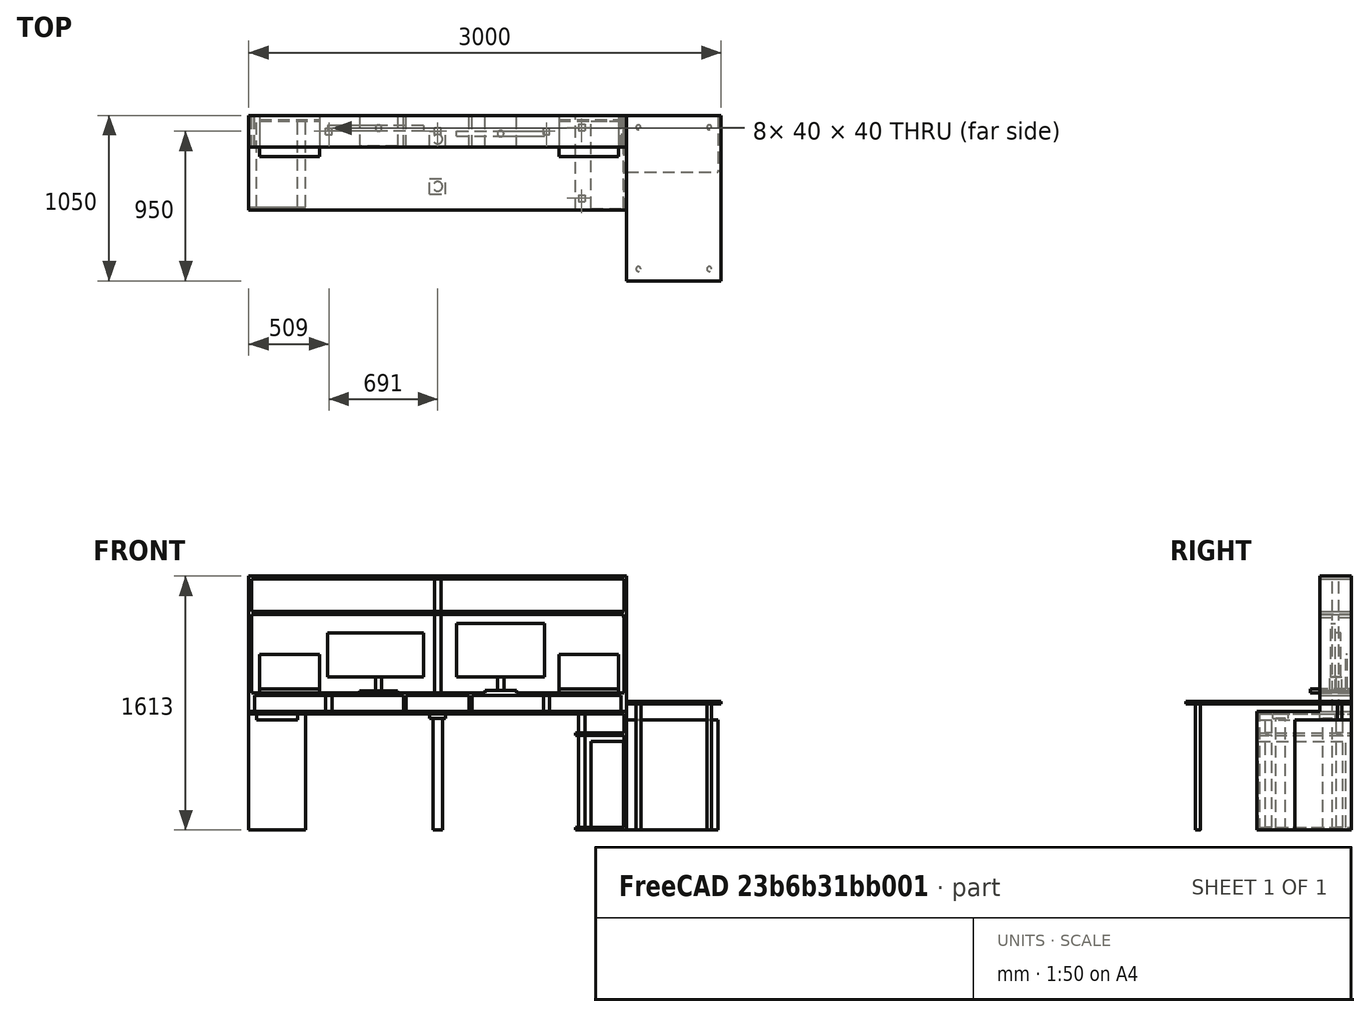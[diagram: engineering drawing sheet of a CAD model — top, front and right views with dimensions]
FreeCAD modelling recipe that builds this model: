
FCSTD DOCUMENT  (FreeCAD 0.16R6712 (Git))
Label: double-desk-240-300
License: All rights reserved
LicenseURL: http://en.wikipedia.org/wiki/All_rights_reserved
objects: Part::Box×43, Part::Cylinder×8, Part::MultiFuse×8, Drawing::FeatureViewPart×4, Drawing::FeaturePage×1
note: 59 computed .brp shape members not serialized (recipe doc carries the construction recipe); baked Part::Feature solids carry a one-line shape summary decoded from their .brp

FEATURE [Part::Box] Box  label="Base"
  Height = 18
  Length = 2400
  Placement = pos=(0,0,736) rot=(0,0,1;0rad)
  Width = 600
FEATURE [Part::Box] Box001  label="IkeaALEX"
  Height = 700
  Length = 360
  Placement = pos=(0,20,0) rot=(0,0,1;0rad)
  Width = 580
FEATURE [Part::Box] Box002  label="R"
  Height = 718
  Length = 18
  Placement = pos=(2382,0,18) rot=(0,0,1;0rad)
  Width = 600
FEATURE [Part::Box] Box003  label="Balda_1"
  Height = 18
  Length = 2364
  Placement = pos=(18,400,854) rot=(0,0,1;0rad)
  Width = 200
FEATURE [Part::Box] Box004  label="Balda_2"
  Height = 18
  Length = 2364
  Placement = pos=(18,400,1369) rot=(0,0,1;0rad)
  Width = 200
FEATURE [Part::Box] Box005  label="Balda_3"
  Height = 18
  Length = 2400
  Placement = pos=(0,400,1595) rot=(0,0,1;0rad)
  Width = 200
FEATURE [Part::Box] Box006  label="Balda_l"
  Height = 841
  Length = 18
  Placement = pos=(0,400,754) rot=(0,0,1;0rad)
  Width = 200
FEATURE [Part::Box] Box007  label="Balda_r"
  Height = 841
  Length = 18
  Placement = pos=(2382,400,754) rot=(0,0,1;0rad)
  Width = 200
FEATURE [Part::Cylinder] Cylinder  label="Leg710C_1"
  Angle = 360
  Height = 710
  Placement = pos=(1200,450,0) rot=(0,0,1;0rad)
  Radius = 30
FEATURE [Part::Cylinder] Cylinder001  label="Leg710C_2"
  Angle = 360
  Height = 710
  Placement = pos=(1200,150,0) rot=(0,0,1;0rad)
  Radius = 30
FEATURE [Part::Box] Box008  label="FixBalda_1l"
  Height = 100
  Length = 18
  Placement = pos=(18,400,754) rot=(0,0,1;0rad)
  Width = 200
FEATURE [Part::Box] Box009  label="FixBalda_1r"
  Height = 100
  Length = 18
  Placement = pos=(2364,400,754) rot=(0,0,1;0rad)
  Width = 200
FEATURE [Part::Box] Box010  label="FixALEX_lb"
  Height = 18
  Length = 50
  Placement = pos=(0,20,700) rot=(0,0,1;0rad)
  Width = 580
FEATURE [Part::Box] Box011  label="FixALEX_lt"
  Height = 18
  Length = 50
  Placement = pos=(0,20,718) rot=(0,0,1;0rad)
  Width = 580
FEATURE [Part::Box] Box012  label="FixALEX_rb"
  Height = 18
  Length = 50
  Placement = pos=(310,20,700) rot=(0,0,1;0rad)
  Width = 580
FEATURE [Part::Box] Box013  label="FixALEX_rt"
  Height = 18
  Length = 50
  Placement = pos=(310,20,718) rot=(0,0,1;0rad)
  Width = 580
FEATURE [Part::Box] Box014  label="FixLeg710C_1b"
  Height = 18
  Length = 100
  Placement = pos=(1150,100,710) rot=(0,0,1;0rad)
  Width = 100
FEATURE [Part::Box] Box015  label="FixLeg710C_2b"
  Height = 18
  Length = 100
  Placement = pos=(1150,400,710) rot=(0,0,1;0rad)
  Width = 100
FEATURE [Part::Box] Box016  label="FixLeg710C_2t"
  Height = 8
  Length = 100
  Placement = pos=(1150,400,728) rot=(0,0,1;0rad)
  Width = 100
FEATURE [Part::Box] Box017  label="FixLeg710C_1t"
  Height = 8
  Length = 100
  Placement = pos=(1150,100,728) rot=(0,0,1;0rad)
  Width = 100
FEATURE [Part::Box] Box018  label="MidBox_l"
  Height = 100
  Length = 18
  Placement = pos=(982,400,754) rot=(0,0,1;0rad)
  Width = 200
FEATURE [Part::Box] Box019  label="MidBox_r"
  Height = 100
  Length = 18
  Placement = pos=(1400,400,754) rot=(0,0,1;0rad)
  Width = 200
FEATURE [Part::Box] Box021  label="FixBalda_1ml"
  Height = 100
  Length = 40
  Placement = pos=(489,480,754) rot=(0,0,1;0rad)
  Width = 40
FEATURE [Part::Box] Box022  label="FixBalda_1mr"
  Height = 100
  Length = 40
  Placement = pos=(1871,480,754) rot=(0,0,1;0rad)
  Width = 40
FEATURE [Part::Box] Box024  label="FixBalda_23"
  Height = 218
  Length = 40
  Placement = pos=(1180,480,1382) rot=(0,0,1;0rad)
  Width = 40
FEATURE [Part::Box] Box025  label="FixBalda_12"
  Height = 507
  Length = 40
  Placement = pos=(1180,480,867) rot=(0,0,1;0rad)
  Width = 40
FEATURE [Part::Box] Box026  label="NZXTWhisper"
  Height = 545
  Length = 205
  Placement = pos=(2175,10,18) rot=(0,0,1;0rad)
  Width = 555
FEATURE [Part::Box] Box027  label="R_b"
  Height = 18
  Length = 325
  Placement = pos=(2075,0,0) rot=(0,0,1;0rad)
  Width = 600
FEATURE [Part::Box] Box028  label="R_f"
  Height = 728
  Length = 40
  Placement = pos=(2095,55,13) rot=(0,0,1;0rad)
  Width = 40
FEATURE [Part::Box] Box029  label="R_r"
  Height = 728
  Length = 40
  Placement = pos=(2095,505,13) rot=(0,0,1;0rad)
  Width = 40
FEATURE [Part::Box] Box030  label="R_m"
  Height = 18
  Length = 307
  Placement = pos=(2075,0,600) rot=(0,0,1;0rad)
  Width = 600
FEATURE [Part::Box] Box031  label="Cube"
  Height = 20
  Length = 1.5
  Width = 200
FEATURE [Part::Box] Box032  label="Cube001"
  Height = 1.5
  Length = 15
  Placement = pos=(0,0,18.5) rot=(0,0,1;0rad)
  Width = 200
FEATURE [Part::MultiFuse] Fusion  label="PletBalda2_l"
  Placement = pos=(18,400,1349) rot=(0,0,1;0rad)
  Shapes = -> [Box031,Box032]
FEATURE [Part::Box] Box033  label="Cube002"
  Height = 20
  Length = 1.5
  Width = 200
FEATURE [Part::Box] Box034  label="Cube003"
  Height = 1.5
  Length = 15
  Placement = pos=(0,0,18.5) rot=(0,0,1;0rad)
  Width = 200
FEATURE [Part::MultiFuse] Fusion001  label="PletBalda2_r"
  Placement = pos=(2382,600,1349) rot=(0,0,1;3.14159rad)
  Shapes = -> [Box033,Box034]
FEATURE [Part::Box] Box035  label="base"
  Height = 25
  Length = 380
  Width = 260
FEATURE [Part::Box] Box036  label="pantalla"
  Height = 240
  Length = 380
  Placement = pos=(0,25,2.5) rot=(0,0,1;0rad)
  Width = 10
FEATURE [Part::MultiFuse] Fusion002  label="PortatilLeire"
  Placement = pos=(450,600,872) rot=(0,0,1;3.14159rad)
  Shapes = -> [Box035,Box036]
FEATURE [Part::Box] Box037  label="pantalla001"
  Height = 340
  Length = 560
  Placement = pos=(-280,70,100) rot=(0,0,1;0rad)
  Width = 30
FEATURE [Part::Box] Box038  label="base001"
  Height = 15
  Length = 200
  Placement = pos=(-100,0,0) rot=(0,0,1;0rad)
  Width = 200
FEATURE [Part::Cylinder] Cylinder002  label="Cilindro"
  Angle = 360
  Height = 90
  Placement = pos=(0,85,10) rot=(0,0,1;0rad)
  Radius = 20
FEATURE [Part::MultiFuse] Fusion003  label="PantallaUnai"
  Placement = pos=(1600,400,872) rot=(0,0,1;0rad)
  Shapes = -> [Box037,Box038,Cylinder002]
FEATURE [Part::Box] Box039  label="pantalla002"
  Height = 280
  Length = 610
  Placement = pos=(-285,60,100) rot=(0,0,1;0rad)
  Width = 35
FEATURE [Part::Cylinder] Cylinder003  label="Cilindro001"
  Angle = 360
  Height = 100
  Placement = pos=(0,75,0) rot=(0,0,1;0rad)
  Radius = 20
FEATURE [Part::Box] Box040  label="base002"
  Height = 10
  Length = 240
  Placement = pos=(-120,0,0) rot=(0,0,1;0rad)
  Width = 190
FEATURE [Part::MultiFuse] Fusion004  label="PantallaLeire"
  Placement = pos=(825,595,872) rot=(0,0,1;3.14159rad)
  Shapes = -> [Box039,Cylinder003,Box040]
FEATURE [Part::Box] Box041  label="base003"
  Height = 25
  Length = 380
  Width = 260
FEATURE [Part::Box] Box042  label="pantalla003"
  Height = 240
  Length = 380
  Placement = pos=(0,25,2.5) rot=(0,0,1;0rad)
  Width = 10
FEATURE [Part::MultiFuse] Fusion005  label="PortatilUnai"
  Placement = pos=(2350,600,872) rot=(0,0,1;3.14159rad)
  Shapes = -> [Box041,Box042]
FEATURE [Part::Box] Box043  label="Cube004"
  Height = 18
  Length = 600
  Placement = pos=(2400,-450,800) rot=(0,0,1;0rad)
  Width = 1050
FEATURE [Part::Cylinder] Cylinder004  label="Cylinder"
  Angle = 360
  Height = 100
  Placement = pos=(2475,525,700) rot=(0,0,1;0rad)
  Radius = 15
FEATURE [Part::Cylinder] Cylinder005  label="Cylinder001"
  Angle = 360
  Height = 800
  Placement = pos=(2475,-375,0) rot=(0,0,1;0rad)
  Radius = 15
FEATURE [Part::Cylinder] Cylinder006  label="Cylinder008"
  Angle = 360
  Height = 100
  Placement = pos=(2925,525,700) rot=(0,0,1;0rad)
  Radius = 15
FEATURE [Part::Cylinder] Cylinder007  label="Cylinder009"
  Angle = 360
  Height = 800
  Placement = pos=(2925,-375,0) rot=(0,0,1;0rad)
  Radius = 15
FEATURE [Part::MultiFuse] Fusion006  label="Aux"
  Shapes = -> [Box043,Cylinder006,Cylinder005,Cylinder007,Cylinder004]
FEATURE [Part::Box] Box044  label="IkeaALEX001"
  Height = 700
  Length = 360
  Placement = pos=(2400,600,0) rot=(0,0,-1;1.5708rad)
  Width = 580
FEATURE [Part::MultiFuse] Fusion007
  Shapes = -> [Box044,Fusion002,Fusion004,Fusion003,Fusion006,Fusion005,Fusion,Fusion001,Box008,Box002,Box022,Box026,Box013,Box029,Box028,Box009,Cylinder,Box015,Box012,Box014,Box004,Box010,Box005,Box007,Box006,Box011,Box021,Box025,Box027,Box017,Box030,Box016,Box,Box001,Cylinder001,Box003,Box018,Box019,Box024]
FEATURE [Drawing::FeatureViewPart] Ortho  label="Ortho_0_0"
  Direction = (0,-1,0)
  HiddenWidth = 0.15
  LineWidth = 0.35
  Rotation = 90
  Scale = 0.055
  ShowHiddenLines = true
  ShowSmoothLines = false
  Source = -> Fusion007
  Tolerance = 0.05
  ViewResult = <blob: 29241 chars omitted>
  Visible = true
  X = 115.25
  Y = 179.357
FEATURE [Drawing::FeatureViewPart] Ortho001  label="Ortho_0_1"
  Direction = (0,0,1)
  HiddenWidth = 0.15
  LineWidth = 0.35
  Rotation = 0
  Scale = 0.055
  ShowHiddenLines = true
  ShowSmoothLines = false
  Source = -> Fusion007
  Tolerance = 0.05
  ViewResult = <blob: 18046 chars omitted>
  Visible = true
  X = 115.25
  Y = 49.125
FEATURE [Drawing::FeatureViewPart] Ortho004  label="Ortho_-1_1"
  Direction = (-0.57735,-0.57735,0.57735)
  HiddenWidth = 0.15
  LineWidth = 0.35
  Rotation = -60
  Scale = 0.03
  ShowHiddenLines = true
  ShowSmoothLines = false
  Source = -> Fusion007
  Tolerance = 0.05
  ViewResult = <blob: 46278 chars omitted>
  Visible = true
  X = 27.5212
  Y = 84.0449
FEATURE [Drawing::FeatureViewPart] Ortho005  label="Ortho_-1_0"
  Direction = (-1,0,0)
  HiddenWidth = 0.15
  LineWidth = 0.35
  Rotation = 90
  Scale = 0.055
  ShowHiddenLines = true
  ShowSmoothLines = false
  Source = -> Fusion007
  Tolerance = 0.05
  ViewResult = <blob: 32065 chars omitted>
  Visible = true
  X = 61.875
  Y = 179.357
FEATURE [Drawing::FeaturePage] Page001
  Group = -> [Ortho,Ortho001,Ortho004,Ortho005]
